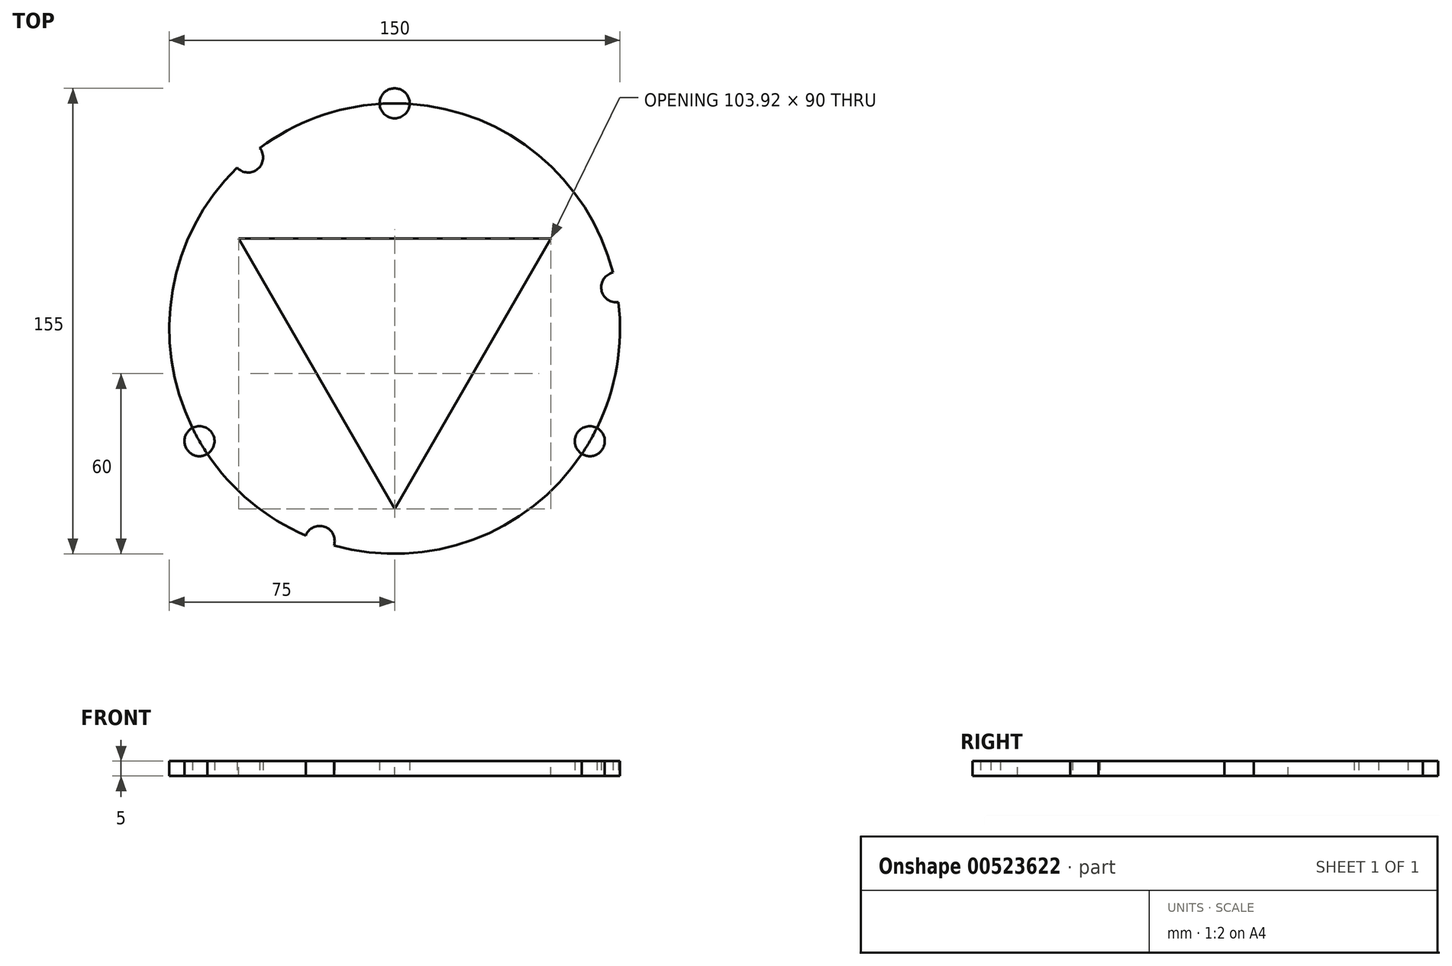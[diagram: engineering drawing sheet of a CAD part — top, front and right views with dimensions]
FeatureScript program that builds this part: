
annotation { "Feature Type Name" : "Feature", "Feature Type Description" : "" }
export const myFeature = defineFeature(function(context is Context, id is Id, definition is map)
    precondition{}
    {
        {
            var Q0;
            Q0=qCreatedBy(makeId("Top.planeOp"),FACE);
            var sketch = newSketch(context, id + "F0", { "sketchPlane" : qUnion([Q0])});
            skCircle(sketch, "E0", {"center": v(0, 0) * mm, "radius": 75 * mm});
            skLineSegment(sketch, "E1", {"start": v(0, 150) * mm, "end": v(-129.9, -75) * mm});
            skLineSegment(sketch, "E2", {"start": v(-129.9, -75) * mm, "end": v(129.9, -75) * mm});
            skLineSegment(sketch, "E3", {"start": v(129.9, -75) * mm, "end": v(0, 150) * mm});
            skText(sketch, "E4", { "text": "Z", "fontName": "OpenSans-Bold.ttf"});
            skText(sketch, "E5", { "text": "Y\n\n", "fontName": "OpenSans-Bold.ttf"});
            skText(sketch, "E6", { "text": "X", "fontName": "OpenSans-Bold.ttf"});
            skPoint(sketch, "E7", {"position": v(0, 75) * mm});
            skPoint(sketch, "E8", {"position": v(-64.95, -37.5) * mm});
            skPoint(sketch, "E9", {"position": v(64.95, -37.5) * mm});
            skLineSegment(sketch, "E10", {"start": v(0, 150) * mm, "end": v(0, 0) * mm});
            skLineSegment(sketch, "E11", {"start": v(0, 0) * mm, "end": v(-129.9, -75) * mm});
            skLineSegment(sketch, "E12", {"start": v(0, 0) * mm, "end": v(129.9, -75) * mm});
            skCircle(sketch, "E13", {"center": v(0, 75) * mm, "radius": 5 * mm});
            skCircle(sketch, "E14", {"center": v(64.95, -37.5) * mm, "radius": 5 * mm});
            skCircle(sketch, "E15", {"center": v(-64.95, -37.5) * mm, "radius": 5 * mm});
            skCircle(sketch, "E16", {"center": v(-24.95, -70.73) * mm, "radius": 5 * mm});
            skCircle(sketch, "E17.1.0", {"center": v(73.73, 13.75) * mm, "radius": 5 * mm});
            skCircle(sketch, "E17.2.0", {"center": v(-48.78, 56.97) * mm, "radius": 5 * mm});
            const initialGuessF0  = {"E4": [-0.04947, 0.15402, 1, 0, 0.01288], "E5": [-0.19281, -0.1153, 1, 0, 0.02408], "E6": [0.16386, -0.11922, 1, 0, 0.02408]};
            skSetInitialGuess(sketch, initialGuessF0);
            skSolve(sketch);
        }
        {
            var Q0;
            {var subQ5=sQuery(id+"F0.wireOp",EDGE,"E0");var subQ6=makeQuery(id+"F0.imprint","INTERSECT",VERTEX,{"derivedFrom":[subQ5,sQuery(id+"F0.wireOp",EDGE,"E1")]});Q0=makeQuery(id+"F0.imprint","IMPRINT",FACE,{"disambiguationData":[TD([[makeQuery(id+"F0.imprint","IMPRINT",EDGE,{"disambiguationData":[TD([[subQ6,1.0]])],"derivedFrom":subQ5}),1.0]])]});}
            var Q1;
            {var subQ5=sQuery(id+"F0.wireOp",EDGE,"E0");var subQ6=makeQuery(id+"F0.imprint","INTERSECT",VERTEX,{"derivedFrom":[subQ5,sQuery(id+"F0.wireOp",EDGE,"E2")]});Q1=makeQuery(id+"F0.imprint","IMPRINT",FACE,{"disambiguationData":[TD([[makeQuery(id+"F0.imprint","IMPRINT",EDGE,{"disambiguationData":[TD([[subQ6,1.0]])],"derivedFrom":subQ5}),1.0]])]});}
            var Q2;
            {var subQ7=sQuery(id+"F0.wireOp",EDGE,"E0");var subQ9=makeQuery(id+"F0.imprint","INTERSECT",VERTEX,{"derivedFrom":[subQ7,sQuery(id+"F0.wireOp",EDGE,"E3")]});Q2=makeQuery(id+"F0.imprint","IMPRINT",FACE,{"disambiguationData":[TD([[makeQuery(id+"F0.imprint","IMPRINT",EDGE,{"disambiguationData":[TD([[subQ9,-1.0]])],"derivedFrom":subQ7}),1.0]])]});}
            var Q3;
            {var subQ0=sQuery(id+"F0.wireOp",EDGE,"E13");var subQ1=sQuery(id+"F0.wireOp",EDGE,"E0");var subQ2=makeQuery(id+"F0.imprint","INTERSECT",VERTEX,{"disambiguationData":[OD(0.0)],"derivedFrom":[subQ1,subQ0]});Q3=makeQuery(id+"F0.imprint","IMPRINT",FACE,{"disambiguationData":[TD([[makeQuery(id+"F0.imprint","IMPRINT",EDGE,{"disambiguationData":[TD([[subQ2,-1.0]])],"derivedFrom":subQ1}),-1.0]])]});}
            var Q4;
            {var subQ0=sQuery(id+"F0.wireOp",EDGE,"E10");var subQ1=sQuery(id+"F0.wireOp",EDGE,"E0");var subQ2=makeQuery(id+"F0.imprint","INTERSECT",VERTEX,{"derivedFrom":[subQ1,subQ0]});Q4=makeQuery(id+"F0.imprint","IMPRINT",FACE,{"disambiguationData":[TD([[makeQuery(id+"F0.imprint","IMPRINT",EDGE,{"disambiguationData":[TD([[subQ2,-1.0]])],"derivedFrom":subQ1}),-1.0]])]});}
            var Q5;
            {var subQ0=sQuery(id+"F0.wireOp",EDGE,"E11");var subQ1=sQuery(id+"F0.wireOp",EDGE,"E0");var subQ2=makeQuery(id+"F0.imprint","INTERSECT",VERTEX,{"derivedFrom":[subQ1,subQ0]});Q5=makeQuery(id+"F0.imprint","IMPRINT",FACE,{"disambiguationData":[TD([[makeQuery(id+"F0.imprint","IMPRINT",EDGE,{"disambiguationData":[TD([[subQ2,-1.0]])],"derivedFrom":subQ1}),-1.0]])]});}
            var Q6;
            {var subQ0=sQuery(id+"F0.wireOp",EDGE,"E15");var subQ1=sQuery(id+"F0.wireOp",EDGE,"E0");var subQ2=makeQuery(id+"F0.imprint","INTERSECT",VERTEX,{"disambiguationData":[OD(0.0)],"derivedFrom":[subQ1,subQ0]});Q6=makeQuery(id+"F0.imprint","IMPRINT",FACE,{"disambiguationData":[TD([[makeQuery(id+"F0.imprint","IMPRINT",EDGE,{"disambiguationData":[TD([[subQ2,-1.0]])],"derivedFrom":subQ1}),-1.0]])]});}
            var Q7;
            {var subQ0=sQuery(id+"F0.wireOp",EDGE,"E14");var subQ1=sQuery(id+"F0.wireOp",EDGE,"E0");var subQ2=makeQuery(id+"F0.imprint","INTERSECT",VERTEX,{"disambiguationData":[OD(0.0)],"derivedFrom":[subQ1,subQ0]});Q7=makeQuery(id+"F0.imprint","IMPRINT",FACE,{"disambiguationData":[TD([[makeQuery(id+"F0.imprint","IMPRINT",EDGE,{"disambiguationData":[TD([[subQ2,-1.0]])],"derivedFrom":subQ1}),-1.0]])]});}
            var Q8;
            {var subQ0=sQuery(id+"F0.wireOp",EDGE,"E12");var subQ1=sQuery(id+"F0.wireOp",EDGE,"E0");var subQ2=makeQuery(id+"F0.imprint","INTERSECT",VERTEX,{"derivedFrom":[subQ1,subQ0]});Q8=makeQuery(id+"F0.imprint","IMPRINT",FACE,{"disambiguationData":[TD([[makeQuery(id+"F0.imprint","IMPRINT",EDGE,{"disambiguationData":[TD([[subQ2,-1.0]])],"derivedFrom":subQ1}),-1.0]])]});}
            extrude(context, id + "F1", {"entities" : qUnion([Q0, Q1, Q2, Q3, Q4, Q5, Q6, Q7, Q8]), "depth" : 5 * mm, "offsetDistance" : 25 * mm});
        }
        {
            var Q0;
            Q0=makeQuery(id+"F1.opExtrude","CAP_FACE",FACE,{"disambiguationData":[OSD([sQuery(id+"F0.wireOp",EDGE,"E0"),sQuery(id+"F0.wireOp",EDGE,"E13"),sQuery(id+"F0.wireOp",EDGE,"E14"),sQuery(id+"F0.wireOp",EDGE,"E15"),sQuery(id+"F0.wireOp",EDGE,"E16"),sQuery(id+"F0.wireOp",EDGE,"E17.1.0"),sQuery(id+"F0.wireOp",EDGE,"E17.2.0")])],"isStart":false});
            var sketch = newSketch(context, id + "F2", { "sketchPlane" : qUnion([Q0])});
            skLineSegment(sketch, "E18", {"start": v(-51.96, 30) * mm, "end": v(0, -60) * mm});
            skPoint(sketch, "E18.startSnap0", {"position": v(-45.52, 53.18) * mm});
            skLineSegment(sketch, "E19", {"start": v(0, -60) * mm, "end": v(51.96, 30) * mm});
            skLineSegment(sketch, "E20", {"start": v(51.96, 30) * mm, "end": v(-51.96, 30) * mm});
            skSolve(sketch);
        }
        {
            var Q0;
            Q0=makeQuery(id+"F2.imprint","IMPRINT",FACE,{"disambiguationData":[TD([[makeQuery(id+"F2.imprint","IMPRINT",EDGE,{"derivedFrom":sQuery(id+"F2.wireOp",EDGE,"E18")}),1.0]])]});
            extrude(context, id + "F3", {"entities" : qUnion([Q0]), "operationType" : NewBodyOperationType.REMOVE, "oppositeDirection" : true, "depth" : 25 * mm, "offsetDistance" : 25 * mm});
        }
    });
